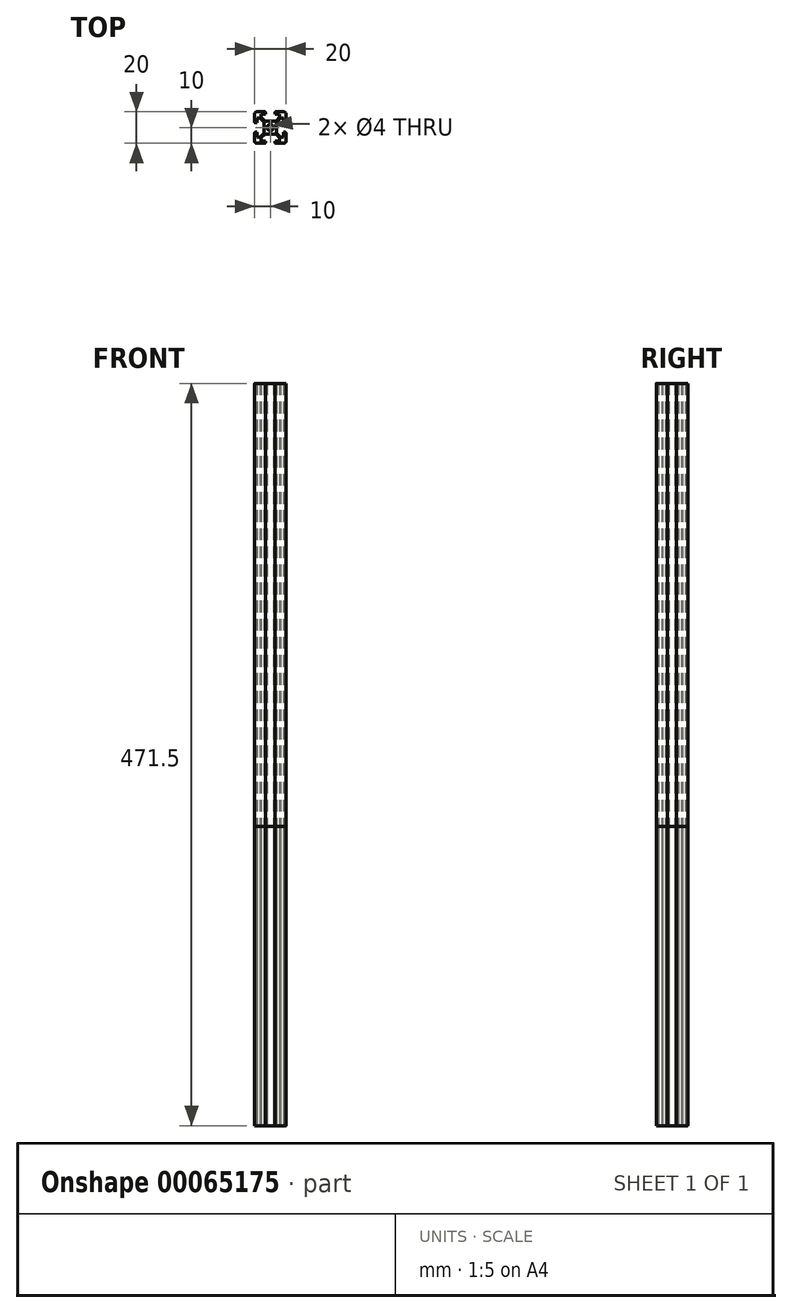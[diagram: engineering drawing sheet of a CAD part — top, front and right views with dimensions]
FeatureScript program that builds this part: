
annotation { "Feature Type Name" : "Feature", "Feature Type Description" : "" }
export const myFeature = defineFeature(function(context is Context, id is Id, definition is map)
    precondition{}
    {
        {
            var Q0;
            Q0=qCreatedBy(makeId("Top.planeOp"),FACE);
            var sketch = newSketch(context, id + "F0", { "sketchPlane" : qUnion([Q0])});
            skCircle(sketch, "E0", {"center": v(0, 0) * mm, "radius": 2 * mm});
            skLineSegment(sketch, "E1", {"start": v(9.5, 3) * mm, "end": v(8.46, 3) * mm});
            skLineSegment(sketch, "E2", {"start": v(8.46, 3) * mm, "end": v(8.46, 6) * mm});
            skLineSegment(sketch, "E3", {"start": v(8.46, 6) * mm, "end": v(6.51, 6) * mm});
            skLineSegment(sketch, "E4", {"start": v(6.51, 6) * mm, "end": v(4, 3.49) * mm});
            skLineSegment(sketch, "E5", {"start": v(4, 3.49) * mm, "end": v(4, 0) * mm});
            skLineSegment(sketch, "E6", {"start": v(10, 8.5) * mm, "end": v(10, 3.5) * mm});
            skLineSegment(sketch, "E7.MirrorCS", {"start": v(3, 9.5) * mm, "end": v(3, 8.46) * mm});
            skLineSegment(sketch, "E8.MirrorCS", {"start": v(8.5, 10) * mm, "end": v(3.5, 10) * mm});
            skLineSegment(sketch, "E9.MirrorCS", {"start": v(3, 8.46) * mm, "end": v(6, 8.46) * mm});
            skLineSegment(sketch, "E10.MirrorCS", {"start": v(6, 6.51) * mm, "end": v(3.49, 4) * mm});
            skLineSegment(sketch, "E11.MirrorCS", {"start": v(3.49, 4) * mm, "end": v(0, 4) * mm});
            skLineSegment(sketch, "E12", {"start": v(6, 8.46) * mm, "end": v(6, 6.51) * mm});
            skPoint(sketch, "E13.visualSharp", {"position": v(10, 10) * mm});
            skArc(sketch, "E13.filletArc", {"start": v(10, 8.5) * mm, "mid": v(9.56, 9.56) * mm, "end": v(8.5, 10) * mm});
            skPoint(sketch, "E14.visualSharp", {"position": v(10, 3) * mm});
            skArc(sketch, "E14.filletArc", {"start": v(9.5, 3) * mm, "mid": v(9.85, 3.15) * mm, "end": v(10, 3.5) * mm});
            skPoint(sketch, "E15.visualSharp", {"position": v(3, 10) * mm});
            skArc(sketch, "E15.filletArc", {"start": v(3.5, 10) * mm, "mid": v(3.15, 9.85) * mm, "end": v(3, 9.5) * mm});
            skLineSegment(sketch, "E16.MirrorCS", {"start": v(-9.5, 3) * mm, "end": v(-8.46, 3) * mm});
            skLineSegment(sketch, "E17.MirrorCS", {"start": v(-8.46, 3) * mm, "end": v(-8.46, 6) * mm});
            skLineSegment(sketch, "E18.MirrorCS", {"start": v(-8.46, 6) * mm, "end": v(-6.51, 6) * mm});
            skLineSegment(sketch, "E19.MirrorCS", {"start": v(-6.51, 6) * mm, "end": v(-4, 3.49) * mm});
            skLineSegment(sketch, "E20.MirrorCS", {"start": v(-10, 8.5) * mm, "end": v(-10, 3.5) * mm});
            skPoint(sketch, "E21.MirrorP", {"position": v(-3, 10) * mm});
            skArc(sketch, "E22.MirrorCS", {"start": v(-10, 8.5) * mm, "mid": v(-9.56, 9.56) * mm, "end": v(-8.5, 10) * mm});
            skArc(sketch, "E23.MirrorCS", {"start": v(-9.5, 3) * mm, "mid": v(-9.85, 3.15) * mm, "end": v(-10, 3.5) * mm});
            skPoint(sketch, "E24.MirrorP", {"position": v(-10, 3) * mm});
            skPoint(sketch, "E25.MirrorP", {"position": v(-10, 10) * mm});
            skLineSegment(sketch, "E26.MirrorCS", {"start": v(-6, 6.51) * mm, "end": v(-3.49, 4) * mm});
            skLineSegment(sketch, "E27.MirrorCS", {"start": v(-3, 9.5) * mm, "end": v(-3, 8.46) * mm});
            skArc(sketch, "E28.MirrorCS", {"start": v(-3.5, 10) * mm, "mid": v(-3.15, 9.85) * mm, "end": v(-3, 9.5) * mm});
            skLineSegment(sketch, "E29.MirrorCS", {"start": v(-3, 8.46) * mm, "end": v(-6, 8.46) * mm});
            skLineSegment(sketch, "E30.MirrorCS", {"start": v(-6, 8.46) * mm, "end": v(-6, 6.51) * mm});
            skLineSegment(sketch, "E31.MirrorCS", {"start": v(-3.49, 4) * mm, "end": v(0, 4) * mm});
            skLineSegment(sketch, "E32.MirrorCS", {"start": v(-8.5, 10) * mm, "end": v(-3.5, 10) * mm});
            skLineSegment(sketch, "E33.MirrorCS", {"start": v(-4, 3.49) * mm, "end": v(-4, 0) * mm});
            skArc(sketch, "E34.MirrorCS", {"start": v(10, -8.5) * mm, "mid": v(9.56, -9.56) * mm, "end": v(8.5, -10) * mm});
            skLineSegment(sketch, "E35.MirrorCS", {"start": v(8.46, -6) * mm, "end": v(6.51, -6) * mm});
            skArc(sketch, "E36.MirrorCS", {"start": v(3.5, -10) * mm, "mid": v(3.15, -9.85) * mm, "end": v(3, -9.5) * mm});
            skLineSegment(sketch, "E37.MirrorCS", {"start": v(-3.49, -4) * mm, "end": v(0, -4) * mm});
            skLineSegment(sketch, "E38.MirrorCS", {"start": v(-3, -9.5) * mm, "end": v(-3, -8.46) * mm});
            skLineSegment(sketch, "E39.MirrorCS", {"start": v(8.5, -10) * mm, "end": v(3.5, -10) * mm});
            skLineSegment(sketch, "E40.MirrorCS", {"start": v(-3, -8.46) * mm, "end": v(-6, -8.46) * mm});
            skArc(sketch, "E41.MirrorCS", {"start": v(-10, -8.5) * mm, "mid": v(-9.56, -9.56) * mm, "end": v(-8.5, -10) * mm});
            skLineSegment(sketch, "E42.MirrorCS", {"start": v(3, -9.5) * mm, "end": v(3, -8.46) * mm});
            skLineSegment(sketch, "E43.MirrorCS", {"start": v(3, -8.46) * mm, "end": v(6, -8.46) * mm});
            skLineSegment(sketch, "E44.MirrorCS", {"start": v(3.49, -4) * mm, "end": v(0, -4) * mm});
            skLineSegment(sketch, "E45.MirrorCS", {"start": v(6, -6.51) * mm, "end": v(3.49, -4) * mm});
            skPoint(sketch, "E46.MirrorP", {"position": v(-3, -10) * mm});
            skPoint(sketch, "E47.MirrorP", {"position": v(3, -10) * mm});
            skPoint(sketch, "E48.MirrorP", {"position": v(10, -10) * mm});
            skLineSegment(sketch, "E49.MirrorCS", {"start": v(-6, -8.46) * mm, "end": v(-6, -6.51) * mm});
            skLineSegment(sketch, "E50.MirrorCS", {"start": v(6, -8.46) * mm, "end": v(6, -6.51) * mm});
            skArc(sketch, "E51.MirrorCS", {"start": v(-3.5, -10) * mm, "mid": v(-3.15, -9.85) * mm, "end": v(-3, -9.5) * mm});
            skPoint(sketch, "E52.MirrorP", {"position": v(-10, -10) * mm});
            skLineSegment(sketch, "E53.MirrorCS", {"start": v(-8.5, -10) * mm, "end": v(-3.5, -10) * mm});
            skLineSegment(sketch, "E54.MirrorCS", {"start": v(-8.46, -6) * mm, "end": v(-6.51, -6) * mm});
            skLineSegment(sketch, "E55.MirrorCS", {"start": v(-6, -6.51) * mm, "end": v(-3.49, -4) * mm});
            skLineSegment(sketch, "E56.MirrorCS", {"start": v(-10, -8.5) * mm, "end": v(-10, -3.5) * mm});
            skLineSegment(sketch, "E57.MirrorCS", {"start": v(-8.46, -3) * mm, "end": v(-8.46, -6) * mm});
            skLineSegment(sketch, "E58.MirrorCS", {"start": v(-6.51, -6) * mm, "end": v(-4, -3.49) * mm});
            skLineSegment(sketch, "E59.MirrorCS", {"start": v(-4, -3.49) * mm, "end": v(-4, 0) * mm});
            skArc(sketch, "E60.MirrorCS", {"start": v(-9.5, -3) * mm, "mid": v(-9.85, -3.15) * mm, "end": v(-10, -3.5) * mm});
            skLineSegment(sketch, "E61.MirrorCS", {"start": v(-9.5, -3) * mm, "end": v(-8.46, -3) * mm});
            skPoint(sketch, "E62.MirrorP", {"position": v(-10, -3) * mm});
            skLineSegment(sketch, "E63.MirrorCS", {"start": v(8.46, -3) * mm, "end": v(8.46, -6) * mm});
            skLineSegment(sketch, "E64.MirrorCS", {"start": v(9.5, -3) * mm, "end": v(8.46, -3) * mm});
            skArc(sketch, "E65.MirrorCS", {"start": v(9.5, -3) * mm, "mid": v(9.85, -3.15) * mm, "end": v(10, -3.5) * mm});
            skLineSegment(sketch, "E66.MirrorCS", {"start": v(6.51, -6) * mm, "end": v(4, -3.49) * mm});
            skPoint(sketch, "E67.MirrorP", {"position": v(10, -3) * mm});
            skLineSegment(sketch, "E68.MirrorCS", {"start": v(4, -3.49) * mm, "end": v(4, 0) * mm});
            skLineSegment(sketch, "E69.MirrorCS", {"start": v(10, -8.5) * mm, "end": v(10, -3.5) * mm});
            skSolve(sketch);
        }
        {
            var Q0;
            Q0=makeQuery(id+"F0.imprint","IMPRINT",FACE,{"disambiguationData":[TD([[makeQuery(id+"F0.imprint","IMPRINT",EDGE,{"derivedFrom":sQuery(id+"F0.wireOp",EDGE,"E0")}),-1.0]])]});
            extrude(context, id + "F1", {"entities" : qUnion([Q0]), "depth" : 190 * mm});
        }
        {
            var Q0;
            Q0=makeQuery(id+"F0.imprint","IMPRINT",FACE,{"disambiguationData":[TD([[makeQuery(id+"F0.imprint","IMPRINT",EDGE,{"derivedFrom":sQuery(id+"F0.wireOp",EDGE,"E0")}),-1.0]])]});
            extrude(context, id + "F2", {"entities" : qUnion([Q0]), "depth" : 471.5 * mm});
        }
    });
